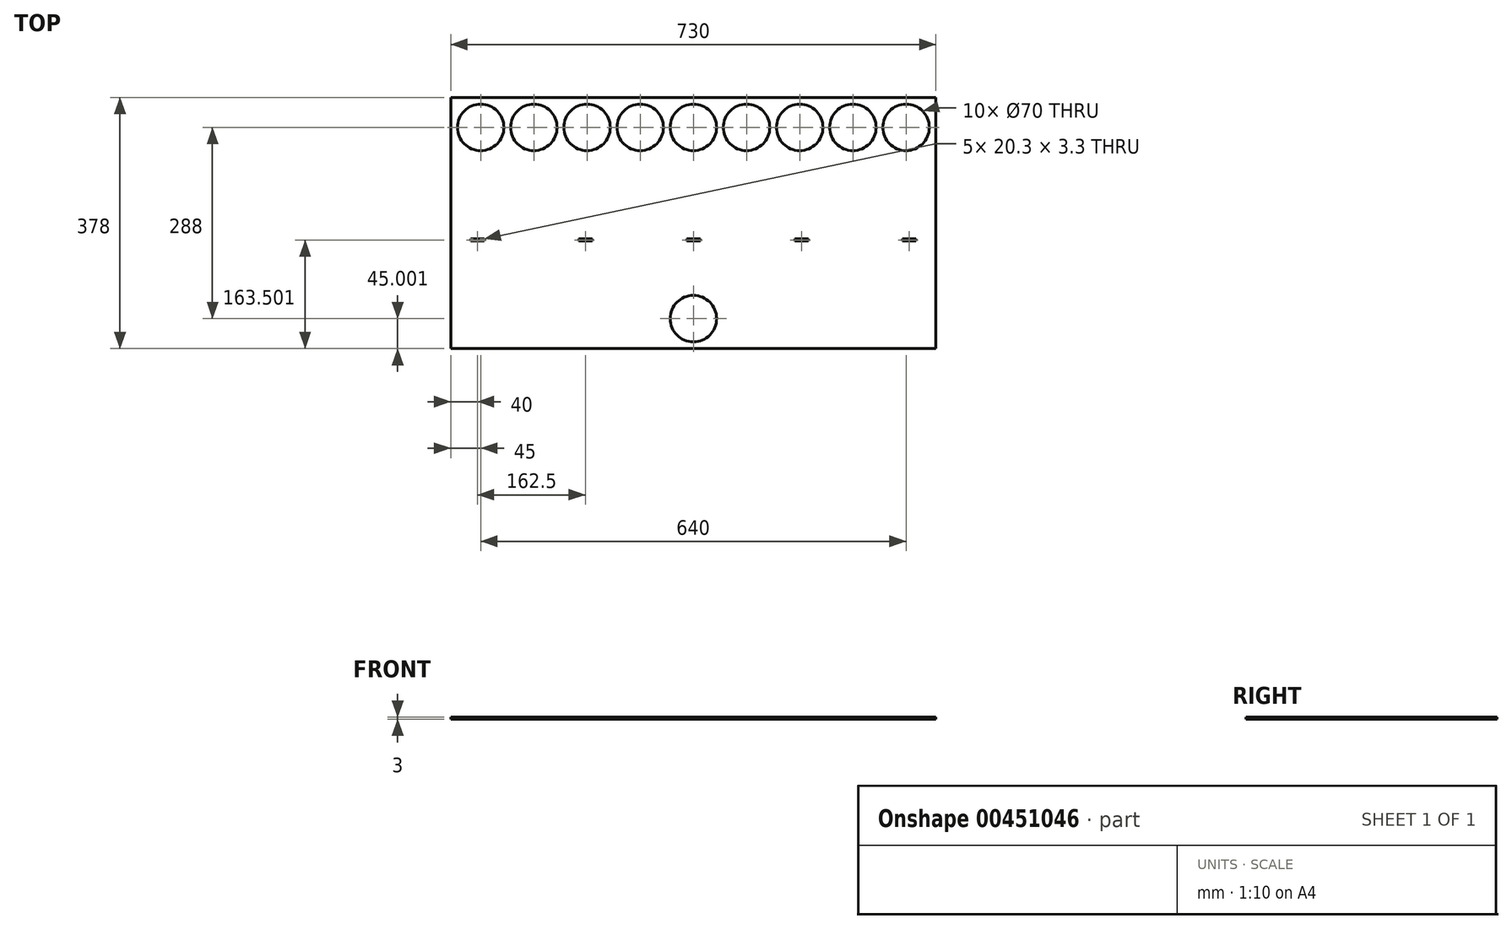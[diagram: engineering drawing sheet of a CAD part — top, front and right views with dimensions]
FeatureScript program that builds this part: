
annotation { "Feature Type Name" : "Feature", "Feature Type Description" : "" }
export const myFeature = defineFeature(function(context is Context, id is Id, definition is map)
    precondition{}
    {
        {
            var Q0;
            Q0=qCreatedBy(makeId("Top.planeOp"),FACE);
            var sketch = newSketch(context, id + "F0", { "sketchPlane" : qUnion([Q0])});
            skLineSegment(sketch, "E0.bottom", {"start": v(-365, 99.13) * mm, "end": v(365, 99.13) * mm});
            skLineSegment(sketch, "E0.top", {"start": v(-365, -278.87) * mm, "end": v(365, -278.87) * mm});
            skLineSegment(sketch, "E0.left", {"start": v(-365, 99.13) * mm, "end": v(-365, -278.87) * mm});
            skLineSegment(sketch, "E0.right", {"start": v(365, 99.13) * mm, "end": v(365, -278.87) * mm});
            skCircle(sketch, "E1", {"center": v(-320, 54.13) * mm, "radius": 35 * mm});
            skCircle(sketch, "E2", {"center": v(0, -233.87) * mm, "radius": 35 * mm});
            skLineSegment(sketch, "E3", {"start": v(0, -278.87) * mm, "end": v(0, -233.87) * mm, "construction": true});
            skCircle(sketch, "E4.1.0.0", {"center": v(-240, 54.13) * mm, "radius": 35 * mm});
            skCircle(sketch, "E4.2.0.0", {"center": v(-160, 54.13) * mm, "radius": 35 * mm});
            skCircle(sketch, "E4.3.0.0", {"center": v(-80, 54.13) * mm, "radius": 35 * mm});
            skCircle(sketch, "E4.4.0.0", {"center": v(0, 54.13) * mm, "radius": 35 * mm});
            skCircle(sketch, "E4.5.0.0", {"center": v(80, 54.13) * mm, "radius": 35 * mm});
            skCircle(sketch, "E4.6.0.0", {"center": v(160, 54.13) * mm, "radius": 35 * mm});
            skCircle(sketch, "E4.7.0.0", {"center": v(240, 54.13) * mm, "radius": 35 * mm});
            skCircle(sketch, "E4.8.0.0", {"center": v(320, 54.13) * mm, "radius": 35 * mm});
            skLineSegment(sketch, "E4.direction1", {"start": v(-320, 54.13) * mm, "end": v(-240, 54.13) * mm, "construction": true});
            skLineSegment(sketch, "E5", {"start": v(-365, 7.13) * mm, "end": v(365, 7.13) * mm, "construction": true});
            skLineSegment(sketch, "E6", {"start": v(365, -186.87) * mm, "end": v(-365, -186.87) * mm, "construction": true});
            skLineSegment(sketch, "E7.bottom", {"start": v(-335.15, -113.72) * mm, "end": v(-314.85, -113.72) * mm});
            skLineSegment(sketch, "E7.top", {"start": v(-335.15, -117.02) * mm, "end": v(-314.85, -117.02) * mm});
            skLineSegment(sketch, "E7.left", {"start": v(-314.85, -113.72) * mm, "end": v(-314.85, -117.02) * mm});
            skLineSegment(sketch, "E7.right", {"start": v(-335.15, -113.72) * mm, "end": v(-335.15, -117.02) * mm});
            skPoint(sketch, "E8.oppositeSnap0", {"position": v(-325, -113.72) * mm});
            skLineSegment(sketch, "E8.bottom", {"start": v(10.15, -117.02) * mm, "end": v(-10.15, -117.02) * mm});
            skLineSegment(sketch, "E8.top", {"start": v(10.15, -113.72) * mm, "end": v(-10.15, -113.72) * mm});
            skLineSegment(sketch, "E8.left", {"start": v(10.15, -117.02) * mm, "end": v(10.15, -113.72) * mm});
            skLineSegment(sketch, "E8.right", {"start": v(-10.15, -117.02) * mm, "end": v(-10.15, -113.72) * mm});
            skLineSegment(sketch, "E9.bottom", {"start": v(314.85, -117.02) * mm, "end": v(335.15, -117.02) * mm});
            skLineSegment(sketch, "E9.top", {"start": v(314.85, -113.72) * mm, "end": v(335.15, -113.72) * mm});
            skLineSegment(sketch, "E9.left", {"start": v(314.85, -117.02) * mm, "end": v(314.85, -113.72) * mm});
            skLineSegment(sketch, "E9.right", {"start": v(335.15, -117.02) * mm, "end": v(335.15, -113.72) * mm});
            skLineSegment(sketch, "E10", {"start": v(0, -117.02) * mm, "end": v(0, -278.87) * mm, "construction": true});
            skLineSegment(sketch, "E11.bottom", {"start": v(-172.65, -117.02) * mm, "end": v(-152.35, -117.02) * mm});
            skLineSegment(sketch, "E11.top", {"start": v(-172.65, -113.72) * mm, "end": v(-152.35, -113.72) * mm});
            skLineSegment(sketch, "E11.left", {"start": v(-152.35, -117.02) * mm, "end": v(-152.35, -113.72) * mm});
            skLineSegment(sketch, "E11.right", {"start": v(-172.65, -117.02) * mm, "end": v(-172.65, -113.72) * mm});
            skLineSegment(sketch, "E12.bottom", {"start": v(152.35, -117.02) * mm, "end": v(172.65, -117.02) * mm});
            skLineSegment(sketch, "E12.top", {"start": v(152.35, -113.72) * mm, "end": v(172.65, -113.72) * mm});
            skLineSegment(sketch, "E12.left", {"start": v(152.35, -117.02) * mm, "end": v(152.35, -113.72) * mm});
            skLineSegment(sketch, "E12.right", {"start": v(172.65, -117.02) * mm, "end": v(172.65, -113.72) * mm});
            skSolve(sketch);
        }
        {
            var Q0;
            Q0=qSketchRegion(id+"F0",true);
            extrude(context, id + "F1", {"entities" : qUnion([Q0]), "depth" : 3 * mm});
        }
    });
